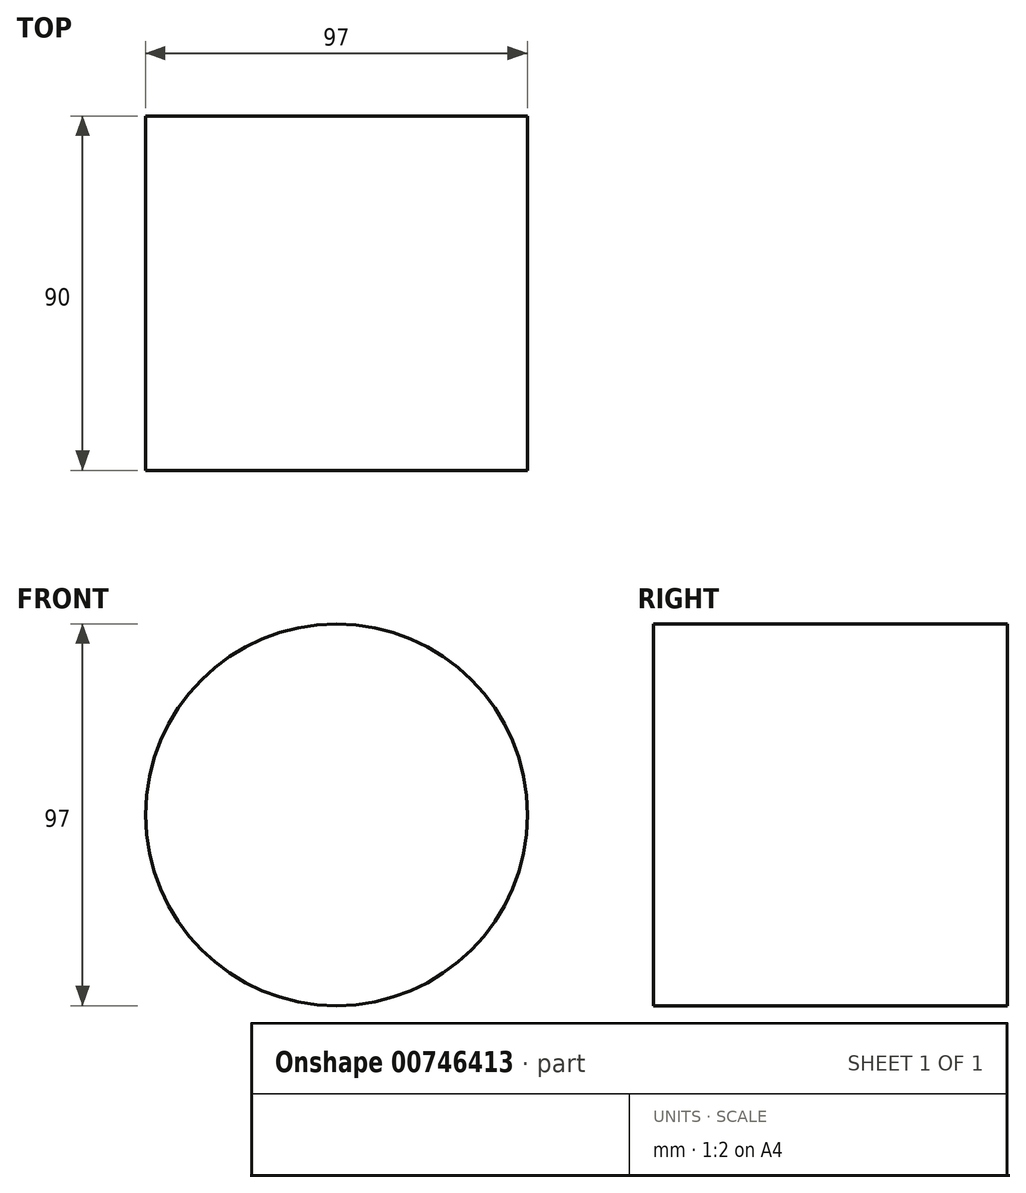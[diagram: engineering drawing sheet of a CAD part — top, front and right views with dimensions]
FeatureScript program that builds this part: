
annotation { "Feature Type Name" : "Feature", "Feature Type Description" : "" }
export const myFeature = defineFeature(function(context is Context, id is Id, definition is map)
    precondition{}
    {
        {
            var Q0;
            Q0=qCreatedBy(makeId("Front.planeOp"),FACE);
            var sketch = newSketch(context, id + "F0", { "sketchPlane" : qUnion([Q0])});
            skCircle(sketch, "E0", {"center": v(1.08, 0) * mm, "radius": 48.5 * mm});
            skSolve(sketch);
        }
        {
            var Q0;
            Q0=makeQuery(id+"F0.imprint","IMPRINT",FACE,{"disambiguationData":[TD([[makeQuery(id+"F0.imprint","IMPRINT",EDGE,{"derivedFrom":sQuery(id+"F0.wireOp",EDGE,"E0")}),1.0]])]});
            extrude(context, id + "F1", {"entities" : qUnion([Q0]), "depth" : 90 * mm, "offsetDistance" : 25 * mm});
        }
    });
